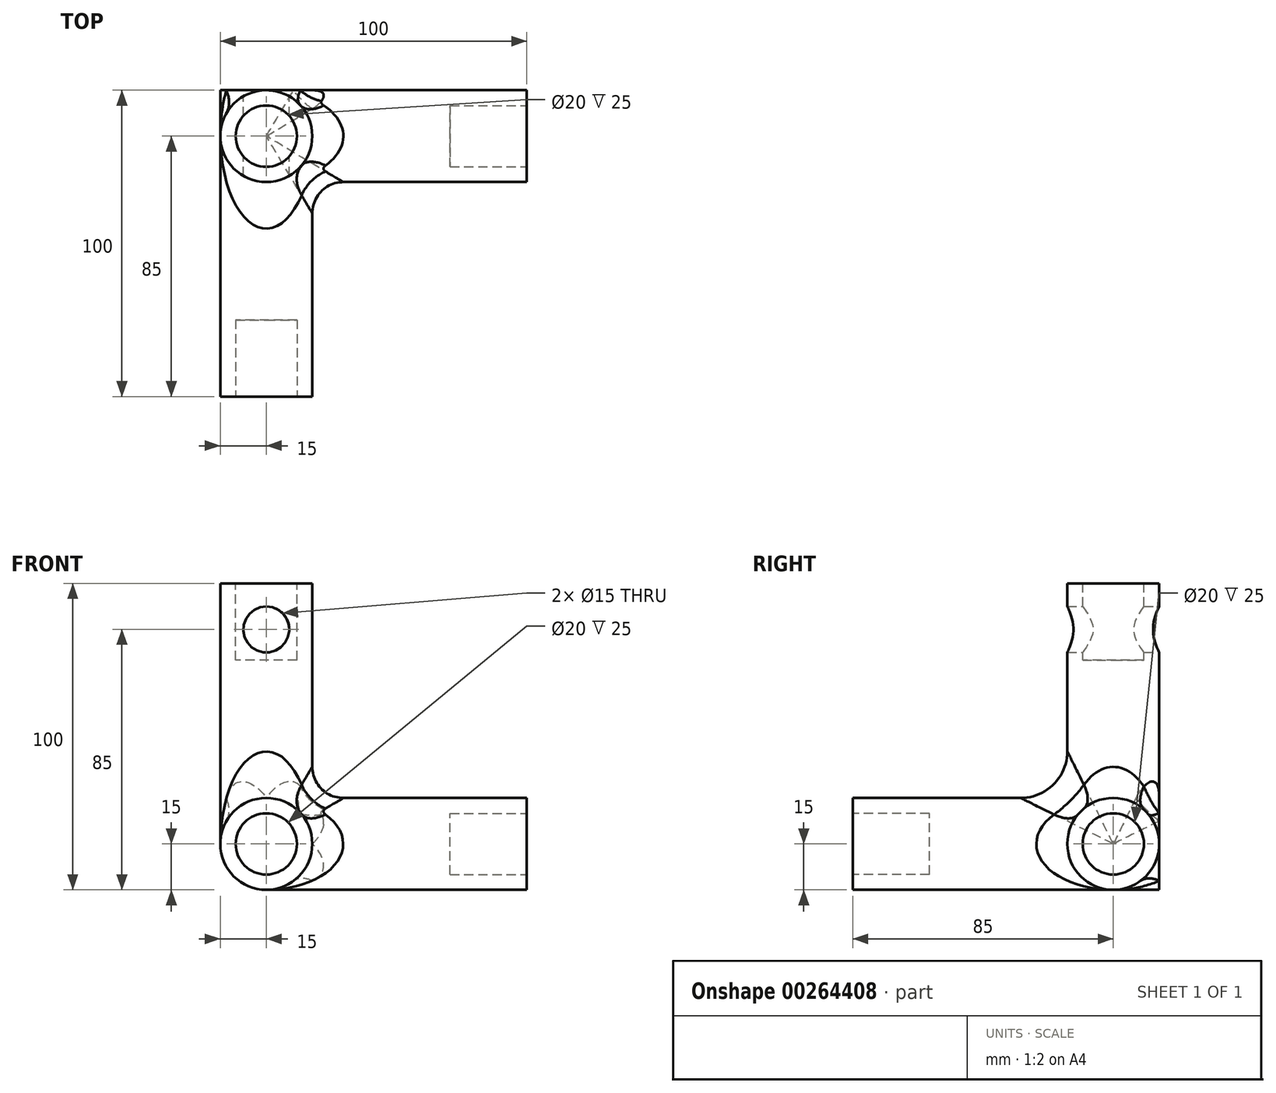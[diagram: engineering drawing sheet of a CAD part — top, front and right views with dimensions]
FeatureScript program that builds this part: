
annotation { "Feature Type Name" : "Feature", "Feature Type Description" : "" }
export const myFeature = defineFeature(function(context is Context, id is Id, definition is map)
    precondition{}
    {
        {
            assignVariable(context, id + "F0", {"name" : "large", "anyValue" : 100});
        }
        {
            assignVariable(context, id + "F1", {"name" : "hole", "anyValue" : 25});
        }
        {
            assignVariable(context, id + "F2", {"name" : "Rex", "anyValue" : 15});
        }
        {
            var Q0;
            Q0=qCreatedBy(makeId("Front.planeOp"),FACE);
            var sketch = newSketch(context, id + "F3", { "sketchPlane" : qUnion([Q0])});
            skCircle(sketch, "E0", {"center": v(0, 0) * mm, "radius": 15 * mm});
            skSolve(sketch);
        }
        {
            var Q0;
            Q0=makeQuery(id+"F3.imprint","IMPRINT",FACE,{"disambiguationData":[TD([[makeQuery(id+"F3.imprint","IMPRINT",EDGE,{"derivedFrom":sQuery(id+"F3.wireOp",EDGE,"E0")}),1.0]])]});
            extrude(context, id + "F4", {"entities" : qUnion([Q0]), "depth" : (getVariable(context, 'large')) * mm});
        }
        {
            var Q0;
            Q0=makeQuery(id+"F4.opExtrude","CAP_FACE",FACE,{"disambiguationData":[OSD([sQuery(id+"F3.wireOp",EDGE,"E0")])],"isStart":false});
            var sketch = newSketch(context, id + "F5", { "sketchPlane" : qUnion([Q0])});
            skCircle(sketch, "E1", {"center": v(0, 0) * mm, "radius": 10 * mm});
            skSolve(sketch);
        }
        {
            var Q0;
            Q0=makeQuery(id+"F5.imprint","IMPRINT",FACE,{"disambiguationData":[TD([[makeQuery(id+"F5.imprint","IMPRINT",EDGE,{"derivedFrom":sQuery(id+"F5.wireOp",EDGE,"E1")}),1.0]])]});
            extrude(context, id + "F6", {"entities" : qUnion([Q0]), "operationType" : NewBodyOperationType.REMOVE, "oppositeDirection" : true, "depth" : (getVariable(context, 'hole')) * mm});
        }
        {
            var Q0;
            Q0=qCreatedBy(makeId("Top.planeOp"),FACE);
            var sketch = newSketch(context, id + "F7", { "sketchPlane" : qUnion([Q0])});
            skPoint(sketch, "E2.middle", {"position": v(0, 0) * mm});
            skCircle(sketch, "E3", {"center": v(0, -15) * mm, "radius": 15 * mm});
            skPoint(sketch, "E3.second.point", {"position": v(0, -30) * mm});
            skPoint(sketch, "E3.third.point", {"position": v(-15, -15) * mm});
            skSolve(sketch);
        }
        {
            var Q0;
            Q0=qSketchRegion(id+"F7",true);
            extrude(context, id + "F8", {"entities" : qUnion([Q0]), "operationType" : NewBodyOperationType.ADD, "depth" : ((.85) * (getVariable(context, 'large'))) * mm});
        }
        {
            var Q0;
            Q0=makeQuery(id+"F8.opExtrude","CAP_FACE",FACE,{"disambiguationData":[OSD([sQuery(id+"F7.wireOp",EDGE,"E3")])],"isStart":false});
            var sketch = newSketch(context, id + "F9", { "sketchPlane" : qUnion([Q0])});
            skCircle(sketch, "E4", {"center": v(0, -15) * mm, "radius": 10 * mm});
            skSolve(sketch);
        }
        {
            var Q0;
            Q0=makeQuery(id+"F9.imprint","IMPRINT",FACE,{"disambiguationData":[TD([[makeQuery(id+"F9.imprint","IMPRINT",EDGE,{"derivedFrom":sQuery(id+"F9.wireOp",EDGE,"E4")}),1.0]])]});
            extrude(context, id + "F10", {"entities" : qUnion([Q0]), "operationType" : NewBodyOperationType.REMOVE, "oppositeDirection" : true, "depth" : (getVariable(context, 'hole')) * mm});
        }
        {
            var Q0;
            Q0=qCreatedBy(makeId("Right.planeOp"),FACE);
            var sketch = newSketch(context, id + "F11", { "sketchPlane" : qUnion([Q0])});
            skCircle(sketch, "E5", {"center": v(-15, 0) * mm, "radius": 15 * mm});
            skPoint(sketch, "E5.third.point", {"position": v(-15, -15) * mm});
            skSolve(sketch);
        }
        {
            var Q0;
            Q0=qSketchRegion(id+"F11",true);
            var Q1;
            Q1=sQuery(id+"F11.wireOp",EDGE,"E5");
            extrude(context, id + "F12", {"entities" : qUnion([Q0]), "operationType" : NewBodyOperationType.ADD, "surfaceEntities" : qUnion([Q1]), "depth" : ((0.85) * (getVariable(context, 'large'))) * mm});
        }
        {
            var Q0;
            Q0=makeQuery(id+"F12.opExtrude","CAP_FACE",FACE,{"disambiguationData":[OSD([sQuery(id+"F11.wireOp",EDGE,"E5")])],"isStart":false});
            var sketch = newSketch(context, id + "F13", { "sketchPlane" : qUnion([Q0])});
            skCircle(sketch, "E6", {"center": v(-15, 0) * mm, "radius": 10 * mm});
            skSolve(sketch);
        }
        {
            var Q0;
            Q0=makeQuery(id+"F13.imprint","IMPRINT",FACE,{"disambiguationData":[TD([[makeQuery(id+"F13.imprint","IMPRINT",EDGE,{"derivedFrom":sQuery(id+"F13.wireOp",EDGE,"E6")}),1.0]])]});
            extrude(context, id + "F14", {"entities" : qUnion([Q0]), "operationType" : NewBodyOperationType.REMOVE, "oppositeDirection" : true, "depth" : (getVariable(context, 'hole')) * mm});
        }
        {
            var Q0;
            Q0=qCreatedBy(makeId("Front.planeOp"),FACE);
            var sketch = newSketch(context, id + "F15", { "sketchPlane" : qUnion([Q0])});
            skLineSegment(sketch, "E7", {"start": v(0, 0) * mm, "end": v(0, 70) * mm});
            skCircle(sketch, "E8", {"center": v(0, 70) * mm, "radius": 7.5 * mm});
            skLineSegment(sketch, "E9", {"start": v(0, 0) * mm, "end": v(0, 85) * mm});
            skSolve(sketch);
        }
        {
            var Q0;
            Q0=makeQuery(id+"F15.imprint","IMPRINT",FACE,{"disambiguationData":[TD([[makeQuery(id+"F15.imprint","IMPRINT",EDGE,{"derivedFrom":sQuery(id+"F15.wireOp",EDGE,"E8")}),1.0]])]});
            extrude(context, id + "F16", {"entities" : qUnion([Q0]), "operationType" : NewBodyOperationType.REMOVE, "depth" : (2 * getVariable(context, 'Rex')) * mm});
        }
        {
            var Q0;
            Q0=makeQuery(id+"F8.boolean.opBoolean","INTERSECT",EDGE,{"disambiguationData":[OD(0.0)],"derivedFrom":[makeQuery(id+"F4.opExtrude","SWEPT_FACE",FACE,{"disambiguationData":[OSD([sQuery(id+"F3.wireOp",EDGE,"E0")])]}),makeQuery(id+"F8.opExtrude","SWEPT_FACE",FACE,{"disambiguationData":[OSD([sQuery(id+"F7.wireOp",EDGE,"E3")])]})]});
            fillet(context, id + "F17", {"entities" : qUnion([Q0]), "radius" : 15.24 * mm, "tangentPropagation" : true, "allowEdgeOverflow" : false});
        }
        {
            var Q0;
            Q0=makeQuery(id+"F12.boolean.opBoolean","INTERSECT",EDGE,{"disambiguationData":[OD(0.0)],"derivedFrom":[makeQuery(id+"F4.opExtrude","SWEPT_FACE",FACE,{"disambiguationData":[OSD([sQuery(id+"F3.wireOp",EDGE,"E0")])]}),makeQuery(id+"F12.opExtrude","SWEPT_FACE",FACE,{"disambiguationData":[OSD([sQuery(id+"F11.wireOp",EDGE,"E5")])]})]});
            fillet(context, id + "F18", {"entities" : qUnion([Q0]), "radius" : 10.16 * mm, "tangentPropagation" : true, "allowEdgeOverflow" : false});
        }
    });
